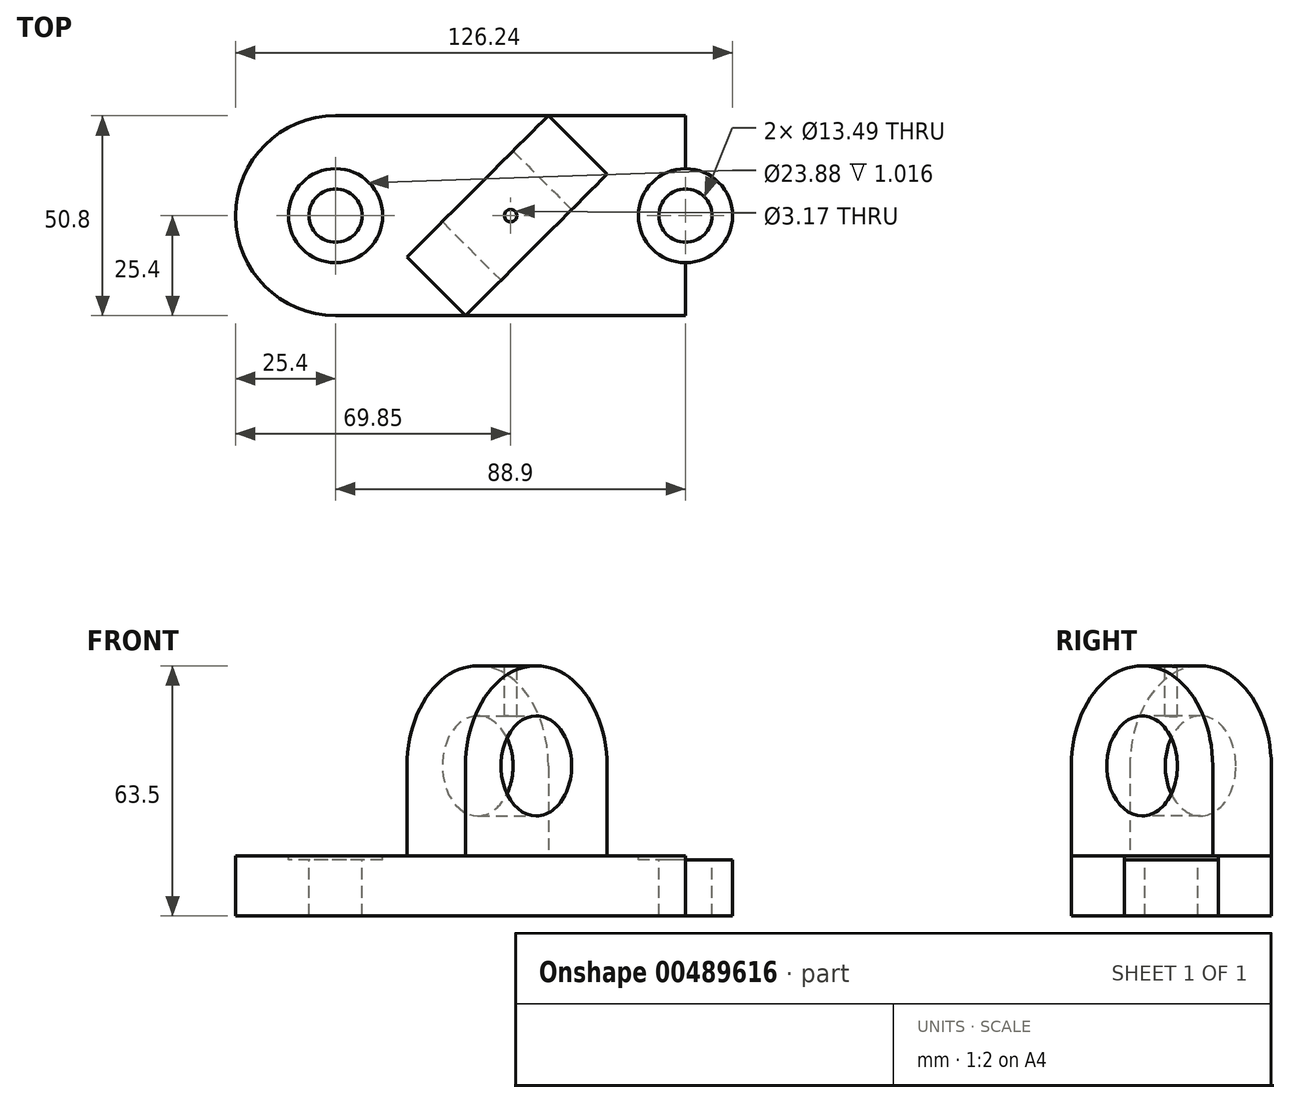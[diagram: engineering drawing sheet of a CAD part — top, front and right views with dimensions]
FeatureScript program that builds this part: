
annotation { "Feature Type Name" : "Feature", "Feature Type Description" : "" }
export const myFeature = defineFeature(function(context is Context, id is Id, definition is map)
    precondition{}
    {
        {
            var Q0;
            Q0=qCreatedBy(makeId("Top.planeOp"),FACE);
            var sketch = newSketch(context, id + "F0", { "sketchPlane" : qUnion([Q0])});
            skLineSegment(sketch, "E0.bottom", {"start": v(-44.45, 25.4) * mm, "end": v(44.45, 25.4) * mm});
            skLineSegment(sketch, "E0.top", {"start": v(-44.45, -25.4) * mm, "end": v(44.45, -25.4) * mm});
            skLineSegment(sketch, "E0.left", {"start": v(-44.45, 25.4) * mm, "end": v(-44.45, -25.4) * mm});
            skLineSegment(sketch, "E0.right", {"start": v(44.45, 25.4) * mm, "end": v(44.45, -25.4) * mm});
            skPoint(sketch, "E0.middle", {"position": v(0, 0) * mm});
            skArc(sketch, "E1", {"start": v(-44.45, 25.4) * mm, "mid": v(-69.85, 0) * mm, "end": v(-44.45, -25.4) * mm});
            skArc(sketch, "E2", {"start": v(44.45, 25.4) * mm, "mid": v(69.85, 0) * mm, "end": v(44.45, -25.4) * mm});
            skCircle(sketch, "E3", {"center": v(-44.45, 0) * mm, "radius": 11.94 * mm});
            skCircle(sketch, "E4", {"center": v(44.45, 0) * mm, "radius": 11.94 * mm});
            skCircle(sketch, "E5", {"center": v(-44.45, 0) * mm, "radius": 6.74 * mm});
            skCircle(sketch, "E6", {"center": v(44.45, 0) * mm, "radius": 6.74 * mm});
            skLineSegment(sketch, "E7", {"start": v(44.45, -25.4) * mm, "end": v(-11.43, -25.4) * mm, "construction": true});
            skLineSegment(sketch, "E8", {"start": v(-11.43, -25.4) * mm, "end": v(24.5, 10.52) * mm});
            skLineSegment(sketch, "E9", {"start": v(24.5, 10.52) * mm, "end": v(9.61, 25.4) * mm});
            skPoint(sketch, "E9.endSnap0", {"position": v(0, 25.4) * mm});
            skLineSegment(sketch, "E10", {"start": v(9.61, 25.4) * mm, "end": v(-26.3, -10.52) * mm});
            skLineSegment(sketch, "E11", {"start": v(-26.3, -10.52) * mm, "end": v(-11.43, -25.4) * mm});
            skSolve(sketch);
        }
        {
            var Q0;
            {var subQ0=sQuery(id+"F0.wireOp",EDGE,"E1");Q0=makeQuery(id+"F0.imprint","IMPRINT",FACE,{"disambiguationData":[TD([[makeQuery(id+"F0.imprint","IMPRINT",EDGE,{"derivedFrom":subQ0}),1.0]])]});}
            var Q1;
            {var subQ9=sQuery(id+"F0.wireOp",EDGE,"E10");Q1=makeQuery(id+"F0.imprint","IMPRINT",FACE,{"disambiguationData":[TD([[makeQuery(id+"F0.imprint","IMPRINT",EDGE,{"derivedFrom":subQ9}),-1.0]])]});}
            var Q2;
            Q2=makeQuery(id+"F0.imprint","IMPRINT",FACE,{"disambiguationData":[TD([[makeQuery(id+"F0.imprint","IMPRINT",EDGE,{"derivedFrom":sQuery(id+"F0.wireOp",EDGE,"E8")}),1.0]])]});
            var Q3;
            {var subQ9=sQuery(id+"F0.wireOp",EDGE,"E8");Q3=makeQuery(id+"F0.imprint","IMPRINT",FACE,{"disambiguationData":[TD([[makeQuery(id+"F0.imprint","IMPRINT",EDGE,{"derivedFrom":subQ9}),-1.0]])]});}
            var Q4;
            {var subQ0=sQuery(id+"F0.wireOp",EDGE,"E2");Q4=makeQuery(id+"F0.imprint","IMPRINT",FACE,{"disambiguationData":[TD([[makeQuery(id+"F0.imprint","IMPRINT",EDGE,{"derivedFrom":subQ0}),-1.0]])]});}
            var Q5;
            {var subQ0=sQuery(id+"F0.wireOp",EDGE,"E4");var subQ1=sQuery(id+"F0.wireOp",EDGE,"E0.right");var subQ2=makeQuery(id+"F0.imprint","INTERSECT",VERTEX,{"disambiguationData":[OD(0.0)],"derivedFrom":[subQ1,subQ0]});Q5=makeQuery(id+"F0.imprint","IMPRINT",FACE,{"disambiguationData":[TD([[makeQuery(id+"F0.imprint","IMPRINT",EDGE,{"disambiguationData":[TD([[subQ2,-1.0]])],"derivedFrom":subQ1}),-1.0]])]});}
            var Q6;
            {var subQ0=sQuery(id+"F0.wireOp",EDGE,"E4");var subQ1=sQuery(id+"F0.wireOp",EDGE,"E0.right");var subQ2=makeQuery(id+"F0.imprint","INTERSECT",VERTEX,{"disambiguationData":[OD(0.0)],"derivedFrom":[subQ1,subQ0]});Q6=makeQuery(id+"F0.imprint","IMPRINT",FACE,{"disambiguationData":[TD([[makeQuery(id+"F0.imprint","IMPRINT",EDGE,{"disambiguationData":[TD([[subQ2,-1.0]])],"derivedFrom":subQ1}),1.0]])]});}
            var Q7;
            {var subQ0=sQuery(id+"F0.wireOp",EDGE,"E3");var subQ1=sQuery(id+"F0.wireOp",EDGE,"E0.left");var subQ2=makeQuery(id+"F0.imprint","INTERSECT",VERTEX,{"disambiguationData":[OD(0.0)],"derivedFrom":[subQ1,subQ0]});Q7=makeQuery(id+"F0.imprint","IMPRINT",FACE,{"disambiguationData":[TD([[makeQuery(id+"F0.imprint","IMPRINT",EDGE,{"disambiguationData":[TD([[subQ2,-1.0]])],"derivedFrom":subQ1}),-1.0]])]});}
            var Q8;
            {var subQ0=sQuery(id+"F0.wireOp",EDGE,"E3");var subQ1=sQuery(id+"F0.wireOp",EDGE,"E0.left");var subQ2=makeQuery(id+"F0.imprint","INTERSECT",VERTEX,{"disambiguationData":[OD(0.0)],"derivedFrom":[subQ1,subQ0]});Q8=makeQuery(id+"F0.imprint","IMPRINT",FACE,{"disambiguationData":[TD([[makeQuery(id+"F0.imprint","IMPRINT",EDGE,{"disambiguationData":[TD([[subQ2,-1.0]])],"derivedFrom":subQ1}),1.0]])]});}
            extrude(context, id + "F1", {"entities" : qUnion([Q0, Q1, Q2, Q3, Q4, Q5, Q6, Q7, Q8]), "oppositeDirection" : true, "depth" : 15.24 * mm});
        }
        {
            var Q0;
            {var subQ0=sQuery(id+"F0.wireOp",EDGE,"E3");var subQ1=sQuery(id+"F0.wireOp",EDGE,"E0.left");var subQ2=makeQuery(id+"F0.imprint","INTERSECT",VERTEX,{"disambiguationData":[OD(0.0)],"derivedFrom":[subQ1,subQ0]});Q0=makeQuery(id+"F0.imprint","IMPRINT",FACE,{"disambiguationData":[TD([[makeQuery(id+"F0.imprint","IMPRINT",EDGE,{"disambiguationData":[TD([[subQ2,-1.0]])],"derivedFrom":subQ1}),1.0]])]});}
            var Q1;
            {var subQ0=sQuery(id+"F0.wireOp",EDGE,"E3");var subQ1=sQuery(id+"F0.wireOp",EDGE,"E0.left");var subQ2=makeQuery(id+"F0.imprint","INTERSECT",VERTEX,{"disambiguationData":[OD(0.0)],"derivedFrom":[subQ1,subQ0]});Q1=makeQuery(id+"F0.imprint","IMPRINT",FACE,{"disambiguationData":[TD([[makeQuery(id+"F0.imprint","IMPRINT",EDGE,{"disambiguationData":[TD([[subQ2,-1.0]])],"derivedFrom":subQ1}),-1.0]])]});}
            var Q2;
            {var subQ0=sQuery(id+"F0.wireOp",EDGE,"E4");var subQ1=sQuery(id+"F0.wireOp",EDGE,"E0.right");var subQ2=makeQuery(id+"F0.imprint","INTERSECT",VERTEX,{"disambiguationData":[OD(0.0)],"derivedFrom":[subQ1,subQ0]});Q2=makeQuery(id+"F0.imprint","IMPRINT",FACE,{"disambiguationData":[TD([[makeQuery(id+"F0.imprint","IMPRINT",EDGE,{"disambiguationData":[TD([[subQ2,-1.0]])],"derivedFrom":subQ1}),1.0]])]});}
            var Q3;
            {var subQ0=sQuery(id+"F0.wireOp",EDGE,"E4");var subQ1=sQuery(id+"F0.wireOp",EDGE,"E0.right");var subQ2=makeQuery(id+"F0.imprint","INTERSECT",VERTEX,{"disambiguationData":[OD(0.0)],"derivedFrom":[subQ1,subQ0]});Q3=makeQuery(id+"F0.imprint","IMPRINT",FACE,{"disambiguationData":[TD([[makeQuery(id+"F0.imprint","IMPRINT",EDGE,{"disambiguationData":[TD([[subQ2,-1.0]])],"derivedFrom":subQ1}),-1.0]])]});}
            extrude(context, id + "F2", {"entities" : qUnion([Q0, Q1, Q2, Q3]), "operationType" : NewBodyOperationType.REMOVE, "oppositeDirection" : true, "depth" : 1.02 * mm});
        }
        {
            var Q0;
            Q0=makeQuery(id+"F0.imprint","IMPRINT",FACE,{"disambiguationData":[TD([[makeQuery(id+"F0.imprint","IMPRINT",EDGE,{"derivedFrom":sQuery(id+"F0.wireOp",EDGE,"E8")}),1.0]])]});
            extrude(context, id + "F3", {"entities" : qUnion([Q0]), "operationType" : NewBodyOperationType.ADD, "depth" : 22.86 * mm});
        }
        {
            var Q0;
            Q0=makeQuery(id+"F3.opExtrude","SWEPT_FACE",FACE,{"disambiguationData":[OSD([sQuery(id+"F0.wireOp",EDGE,"E8")])]});
            var sketch = newSketch(context, id + "F4", { "sketchPlane" : qUnion([Q0])});
            skArc(sketch, "E12", {"start": v(24.76, 22.86) * mm, "mid": v(-0.64, 48.26) * mm, "end": v(-26.04, 22.86) * mm});
            skCircle(sketch, "E13", {"center": v(-0.64, 22.86) * mm, "radius": 12.7 * mm});
            skSolve(sketch);
        }
        {
            var Q0;
            {var subQ0=sQuery(id+"F4.wireOp",EDGE,"E12");Q0=makeQuery(id+"F4.imprint","IMPRINT",FACE,{"disambiguationData":[TD([[makeQuery(id+"F4.imprint","IMPRINT",EDGE,{"derivedFrom":subQ0}),1.0]])]});}
            var Q1;
            Q1=makeQuery(id+"F3.opExtrude","SWEPT_FACE",FACE,{"disambiguationData":[OSD([sQuery(id+"F0.wireOp",EDGE,"E10")])]});
            extrude(context, id + "F5", {"entities" : qUnion([Q0]), "operationType" : NewBodyOperationType.ADD, "endBound" : BoundingType.UP_TO_SURFACE, "oppositeDirection" : true, "endBoundEntityFace" : qUnion([Q1]), "depth" : 25.4 * mm});
        }
        {
            var Q0;
            {var subQ0=sQuery(id+"F4.wireOp",EDGE,"E13");var subQ1=makeQuery(id+"F3.opExtrude","CAP_EDGE",EDGE,{"disambiguationData":[OSD([sQuery(id+"F0.wireOp",EDGE,"E8")])],"isStart":false});var subQ2=makeQuery(id+"F4.imprint","INTERSECT",VERTEX,{"disambiguationData":[OD(0.0)],"derivedFrom":[subQ1,subQ0]});Q0=makeQuery(id+"F4.imprint","IMPRINT",FACE,{"disambiguationData":[TD([[makeQuery(id+"F4.imprint","IMPRINT",EDGE,{"disambiguationData":[TD([[subQ2,-1.0]])],"derivedFrom":subQ0}),1.0]])]});}
            extrude(context, id + "F6", {"entities" : qUnion([Q0]), "operationType" : NewBodyOperationType.REMOVE, "endBound" : BoundingType.THROUGH_ALL, "oppositeDirection" : true, "depth" : 25.4 * mm});
        }
        {
            var Q0;
            Q0=qCreatedBy(makeId("Top.planeOp"),FACE);
            cPlane(context, id + "F7", {"entities" : qUnion([Q0]), "cplaneType" : CPlaneType.OFFSET, "offset" : 48.26 * mm, "width" : 152.4 * mm, "height" : 152.4 * mm});
        }
        {
            var Q0;
            Q0=qCreatedBy(id+"F7.planeOp",FACE);
            var sketch = newSketch(context, id + "F8", { "sketchPlane" : qUnion([Q0])});
            skCircle(sketch, "E14", {"center": v(0, 0) * mm, "radius": 1.59 * mm});
            skSolve(sketch);
        }
        {
            var Q0;
            Q0 = qSketchRegion(id + "F8", true);
            extrude(context, id + "F9", {"entities" : qUnion([Q0]), "operationType" : NewBodyOperationType.REMOVE, "oppositeDirection" : true, "depth" : 25.4 * mm});
        }
    });
